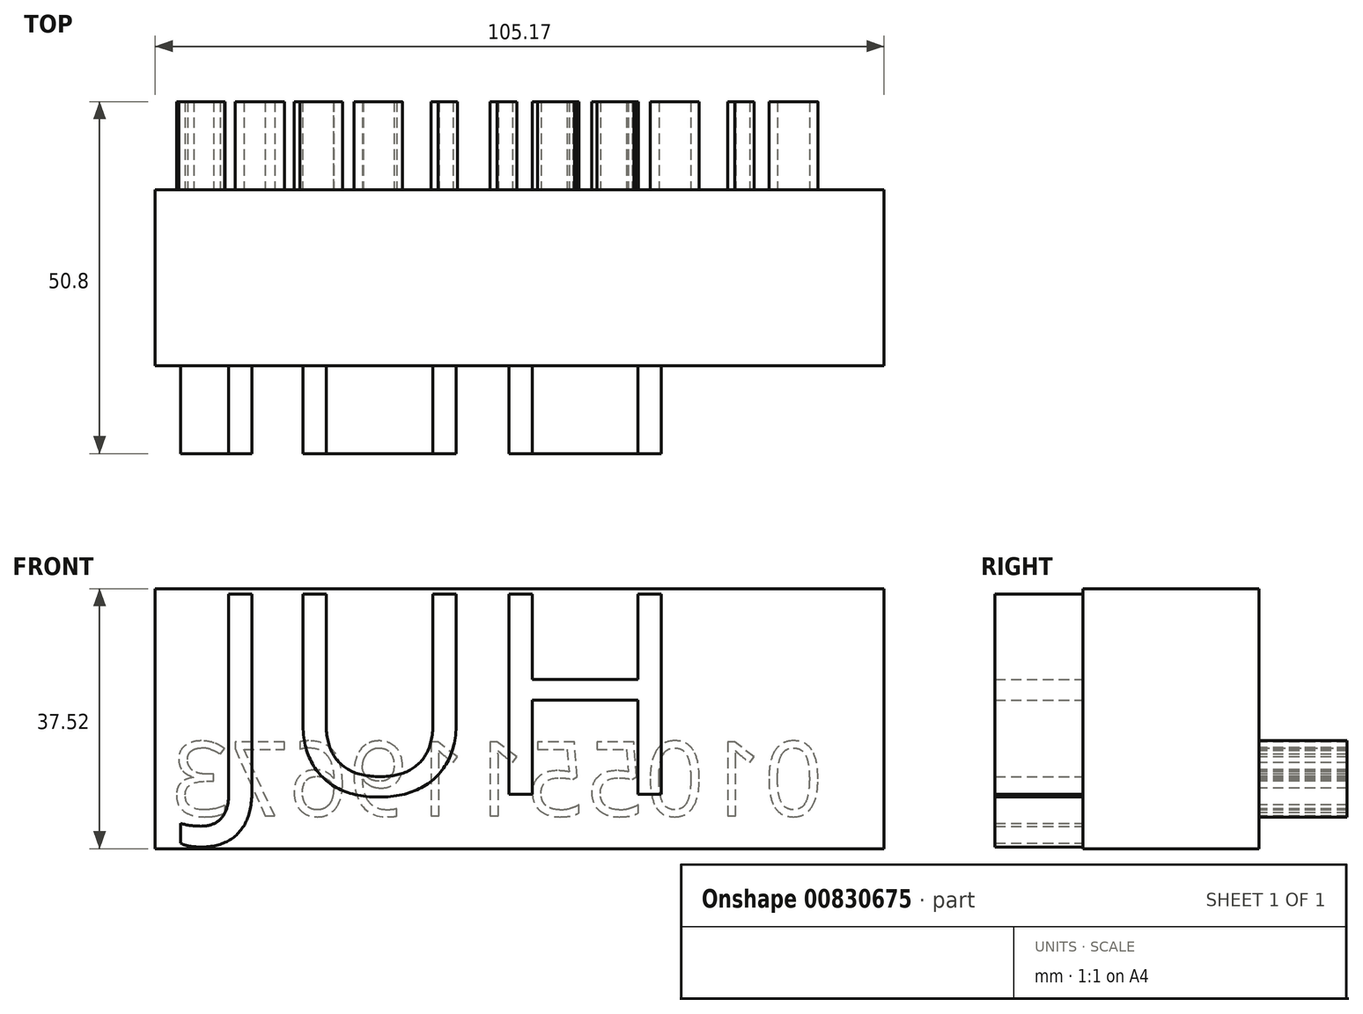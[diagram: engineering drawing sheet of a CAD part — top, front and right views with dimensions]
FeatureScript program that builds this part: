
annotation { "Feature Type Name" : "Feature", "Feature Type Description" : "" }
export const myFeature = defineFeature(function(context is Context, id is Id, definition is map)
    precondition{}
    {
        {
            var Q0;
            Q0=qCreatedBy(makeId("Front.planeOp"),FACE);
            var sketch = newSketch(context, id + "F0", { "sketchPlane" : qUnion([Q0])});
            skLineSegment(sketch, "E0.bottom", {"start": v(0, 0) * mm, "end": v(105.17, 0) * mm});
            skLineSegment(sketch, "E0.top", {"start": v(0, 37.52) * mm, "end": v(105.17, 37.52) * mm});
            skLineSegment(sketch, "E0.left", {"start": v(0, 0) * mm, "end": v(0, 37.52) * mm});
            skLineSegment(sketch, "E0.right", {"start": v(105.17, 0) * mm, "end": v(105.17, 37.52) * mm});
            skSolve(sketch);
        }
        {
            var Q0;
            Q0 = qSketchRegion(id + "F0", true);
            extrude(context, id + "F1", {"entities" : qUnion([Q0]), "depth" : 25.4 * mm, "offsetDistance" : 25.4 * mm});
        }
        {
            var Q0;
            Q0=makeQuery(id+"F1.opExtrude","CAP_FACE",FACE,{"disambiguationData":[OSD([sQuery(id+"F0.wireOp",EDGE,"E0.bottom"),sQuery(id+"F0.wireOp",EDGE,"E0.top"),sQuery(id+"F0.wireOp",EDGE,"E0.left"),sQuery(id+"F0.wireOp",EDGE,"E0.right")])],"isStart":false});
            var sketch = newSketch(context, id + "F2", { "sketchPlane" : qUnion([Q0])});
            skText(sketch, "E1", { "text": "JUH", "fontName": "OpenSans-Regular.ttf"});
            const initialGuessF2  = {"E1": [0.00684, 0.00784, 1, 0, 0.02913]};
            skSetInitialGuess(sketch, initialGuessF2);
            skSolve(sketch);
        }
        {
            var Q0;
            Q0 = qSketchRegion(id + "F2", true);
            extrude(context, id + "F3", {"entities" : qUnion([Q0]), "operationType" : NewBodyOperationType.ADD, "depth" : 12.7 * mm, "offsetDistance" : 25.4 * mm});
        }
        {
            var Q0;
            Q0=makeQuery(id+"F1.opExtrude","CAP_FACE",FACE,{"disambiguationData":[OSD([sQuery(id+"F0.wireOp",EDGE,"E0.bottom"),sQuery(id+"F0.wireOp",EDGE,"E0.top"),sQuery(id+"F0.wireOp",EDGE,"E0.left"),sQuery(id+"F0.wireOp",EDGE,"E0.right")])],"isStart":true});
            var sketch = newSketch(context, id + "F4", { "sketchPlane" : qUnion([Q0])});
            skSolve(sketch);
        }
        {
            var Q0;
            Q0=makeQuery(id+"F4.imprint","IMPRINT",FACE,{"disambiguationData":[TD([[makeQuery(id+"F4.imprint","IMPRINT",EDGE,{"derivedFrom":makeQuery(id+"F1.opExtrude","CAP_EDGE",EDGE,{"disambiguationData":[OSD([sQuery(id+"F0.wireOp",EDGE,"E0.bottom")])],"isStart":true})}),-1.0]])]});
            var sketch = newSketch(context, id + "F5", { "sketchPlane" : qUnion([Q0])});
            skText(sketch, "E2", { "text": "01055119673", "fontName": "OpenSans-Regular.ttf"});
            const initialGuessF5  = {"E2": [-0.09636, 0.00472, 1, 0, 0.01078]};
            skSetInitialGuess(sketch, initialGuessF5);
            skSolve(sketch);
        }
        {
            var Q0;
            Q0 = qSketchRegion(id + "F5", true);
            extrude(context, id + "F6", {"entities" : qUnion([Q0]), "operationType" : NewBodyOperationType.ADD, "depth" : 12.7 * mm, "offsetDistance" : 25.4 * mm});
        }
        {
            var Q0;
            Q0 = qSketchRegion(id + "F5", true);
            extrude(context, id + "F7", {"entities" : qUnion([Q0]), "operationType" : NewBodyOperationType.ADD, "depth" : 12.7 * mm, "offsetDistance" : 25.4 * mm});
        }
    });
